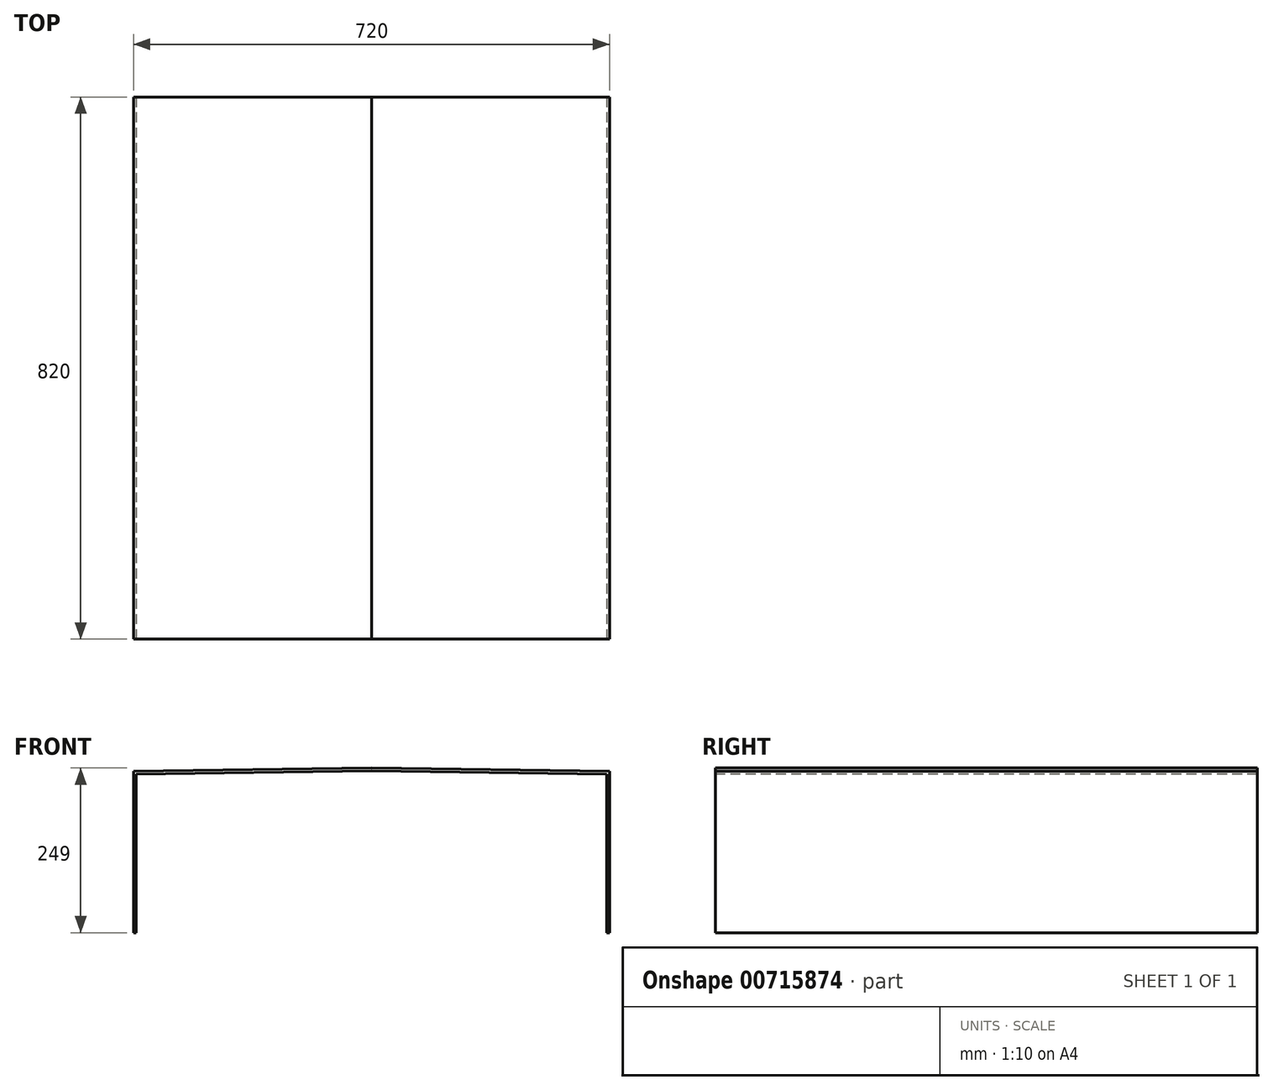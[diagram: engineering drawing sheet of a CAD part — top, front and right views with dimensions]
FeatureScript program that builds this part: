
annotation { "Feature Type Name" : "Feature", "Feature Type Description" : "" }
export const myFeature = defineFeature(function(context is Context, id is Id, definition is map)
    precondition{}
    {
        {
            var Q0;
            Q0=qCreatedBy(makeId("Front.planeOp"),FACE);
            var sketch = newSketch(context, id + "F0", { "sketchPlane" : qUnion([Q0])});
            skLineSegment(sketch, "E0.bottom", {"start": v(0, 0) * mm, "end": v(720, 0) * mm});
            skLineSegment(sketch, "E0.top", {"start": v(0, 244) * mm, "end": v(720, 244) * mm});
            skLineSegment(sketch, "E0.left", {"start": v(0, 0) * mm, "end": v(0, 244) * mm});
            skLineSegment(sketch, "E0.right", {"start": v(720, 0) * mm, "end": v(720, 244) * mm});
            skLineSegment(sketch, "E1", {"start": v(0, 244) * mm, "end": v(360, 249) * mm});
            skPoint(sketch, "E1.endSnap0", {"position": v(360, 244) * mm});
            skLineSegment(sketch, "E2", {"start": v(360, 249) * mm, "end": v(720, 244) * mm});
            skSolve(sketch);
        }
        {
            var Q0;
            Q0 = qSketchRegion(id + "F0", true);
            extrude(context, id + "F1", {"entities" : qUnion([Q0]), "oppositeDirection" : true, "depth" : 820 * mm, "offsetDistance" : 25 * mm});
        }
        {
            var Q0;
            Q0=qCreatedBy(makeId("Front.planeOp"),FACE);
            var sketch = newSketch(context, id + "F2", { "sketchPlane" : qUnion([Q0])});
            skLineSegment(sketch, "E3", {"start": v(4, 0) * mm, "end": v(4, 240.06) * mm});
            skLineSegment(sketch, "E4", {"start": v(716, 240.06) * mm, "end": v(716, 0) * mm});
            skLineSegment(sketch, "E5", {"start": v(716, 0) * mm, "end": v(4, 0) * mm});
            skLineSegment(sketch, "E6", {"start": v(360, 379.26) * mm, "end": v(360, -56.6) * mm, "construction": true});
            skLineSegment(sketch, "E7", {"start": v(4, 240.06) * mm, "end": v(360, 245) * mm});
            skLineSegment(sketch, "E8", {"start": v(360, 245) * mm, "end": v(716, 240.06) * mm});
            skSolve(sketch);
        }
        {
            var Q0;
            Q0 = qSketchRegion(id + "F2", true);
            extrude(context, id + "F3", {"entities" : qUnion([Q0]), "operationType" : NewBodyOperationType.REMOVE, "oppositeDirection" : true, "depth" : 830 * mm, "offsetDistance" : 25 * mm});
        }
    });
